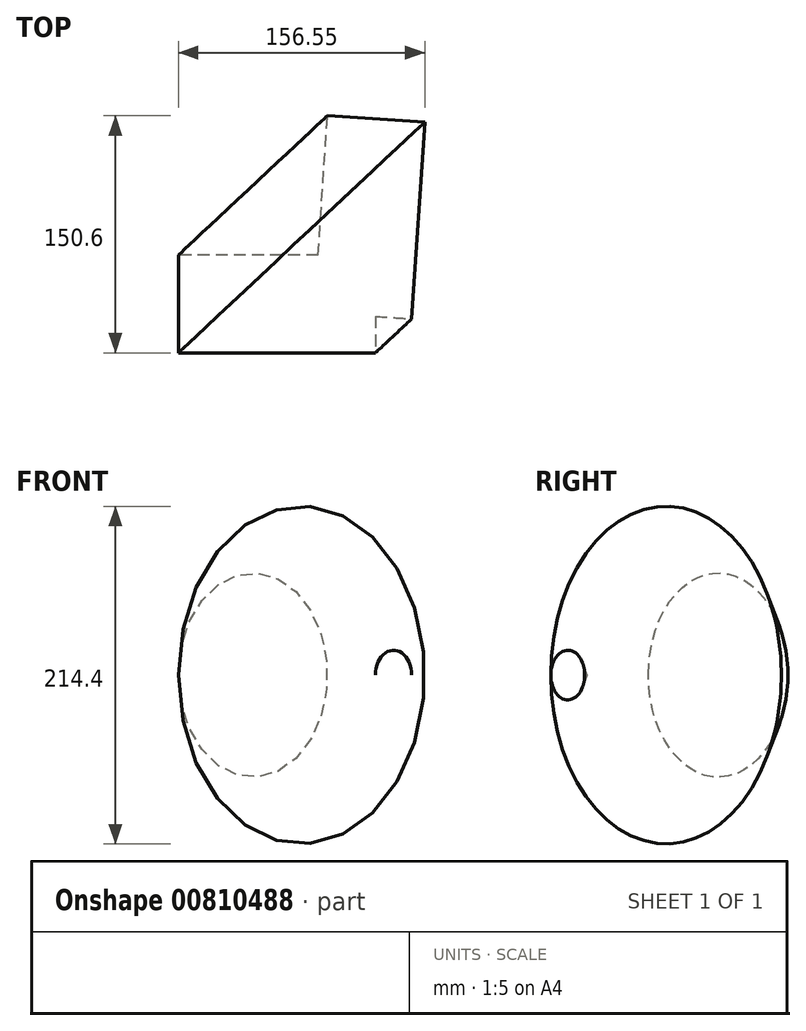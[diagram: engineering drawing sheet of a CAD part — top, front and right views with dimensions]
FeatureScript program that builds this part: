
annotation { "Feature Type Name" : "Feature", "Feature Type Description" : "" }
export const myFeature = defineFeature(function(context is Context, id is Id, definition is map)
    precondition{}
    {
        {
            var Q0;
            Q0=qCreatedBy(makeId("Top.planeOp"),FACE);
            var sketch = newSketch(context, id + "F0", { "sketchPlane" : qUnion([Q0])});
            skLineSegment(sketch, "E0.bottom", {"start": v(-60.62, 38.33) * mm, "end": v(64.59, 38.33) * mm});
            skLineSegment(sketch, "E0.top", {"start": v(-60.62, -23.67) * mm, "end": v(64.59, -23.67) * mm});
            skLineSegment(sketch, "E0.left", {"start": v(-60.62, 38.33) * mm, "end": v(-60.62, -23.67) * mm});
            skLineSegment(sketch, "E0.right", {"start": v(64.59, 38.33) * mm, "end": v(64.59, -23.67) * mm});
            skLineSegment(sketch, "E1", {"start": v(22.75, 44.13) * mm, "end": v(71.61, -8.1) * mm});
            skSolve(sketch);
        }
        {
            var Q0;
            {var subQ1=sQuery(id+"F0.wireOp",EDGE,"E0.top");Q0=makeQuery(id+"F0.imprint","IMPRINT",FACE,{"disambiguationData":[TD([[makeQuery(id+"F0.imprint","IMPRINT",EDGE,{"derivedFrom":subQ1}),1.0]])]});}
            var Q1;
            Q1=sQuery(id+"F0.wireOp",EDGE,"E1");
            revolve(context, id + "F1", {"surfaceOperationType" : NewSurfaceOperationType.NEW, "entities" : qUnion([Q0]), "axis" : qUnion([Q1]), "revolveType" : RevolveType.FULL});
        }
    });
